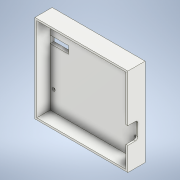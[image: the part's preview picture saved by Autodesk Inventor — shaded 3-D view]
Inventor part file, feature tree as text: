
AUTODESK INVENTOR PART (.ipt)
format: ipt  version: 2022 (Build 260153000, 153)  size: 130,048 bytes
history: imported  units: in
note: dims shown in document units (in); Inventor stores cm internally (conversion verified against a paired STEP export)
features: imported_body x1
ambient origin geometry x8: Origin, YZ Plane, XZ Plane, XY Plane, X Axis, Y Axis, Z Axis, Center Point
bodies: Solid1 (imported_parasolid), Body2 (imported_parasolid)
feature tree (1):
  imported_body  NMx_Import_Brep_tag  [imported B-rep: ~56 faces, bbox_mm=[99.0, 93.6, 18.35]]
